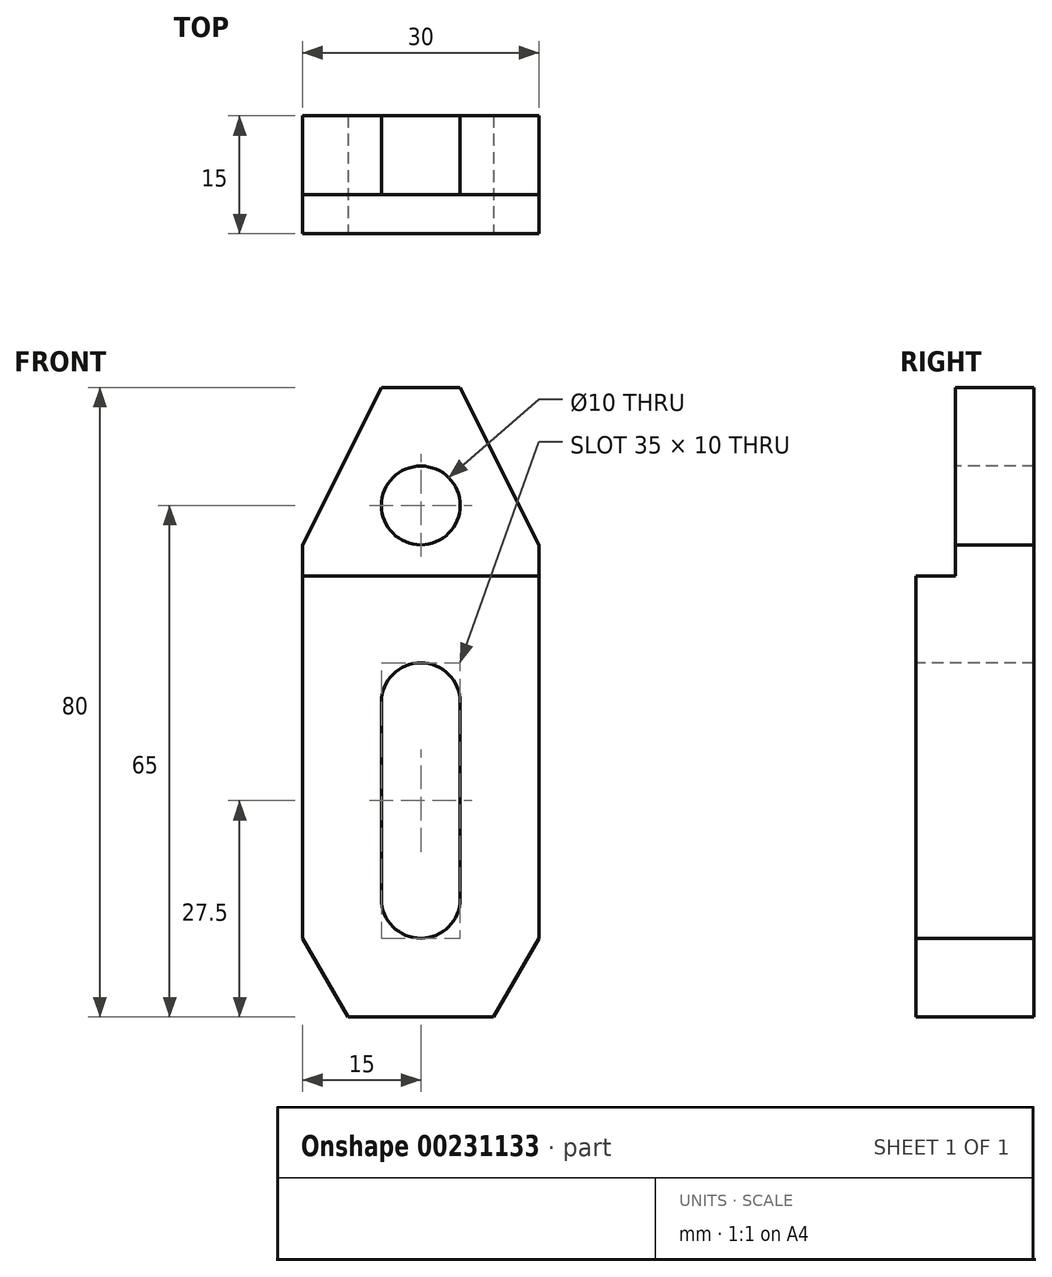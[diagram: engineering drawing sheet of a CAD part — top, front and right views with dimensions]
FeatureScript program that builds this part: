
annotation { "Feature Type Name" : "Feature", "Feature Type Description" : "" }
export const myFeature = defineFeature(function(context is Context, id is Id, definition is map)
    precondition{}
    {
        {
            var Q0;
            Q0=qCreatedBy(makeId("Right.planeOp"),FACE);
            var sketch = newSketch(context, id + "F0", { "sketchPlane" : qUnion([Q0])});
            skLineSegment(sketch, "E0", {"start": v(10, 66) * mm, "end": v(10, 10) * mm});
            skLineSegment(sketch, "E1", {"start": v(10, 10) * mm, "end": v(25, 10) * mm});
            skLineSegment(sketch, "E2", {"start": v(25, 10) * mm, "end": v(25, 90) * mm});
            skLineSegment(sketch, "E3", {"start": v(25, 90) * mm, "end": v(15, 90) * mm});
            skLineSegment(sketch, "E4", {"start": v(15, 90) * mm, "end": v(15, 66) * mm});
            skLineSegment(sketch, "E5", {"start": v(15, 66) * mm, "end": v(10, 66) * mm});
            skSolve(sketch);
        }
        {
            var Q0;
            Q0 = qSketchRegion(id + "F0", true);
            extrude(context, id + "F1", {"entities" : qUnion([Q0]), "depth" : 30 * mm});
        }
        {
            var Q0;
            Q0=makeQuery(id+"F1.opExtrude","SWEPT_FACE",FACE,{"disambiguationData":[OSD([sQuery(id+"F0.wireOp",EDGE,"E0")])]});
            var sketch = newSketch(context, id + "F2", { "sketchPlane" : qUnion([Q0])});
            skLineSegment(sketch, "E6.0.0", {"start": v(0, 66) * mm, "end": v(0, 10) * mm, "construction": true});
            skLineSegment(sketch, "E6.0.1", {"start": v(0, 10) * mm, "end": v(30, 10) * mm, "construction": true});
            skLineSegment(sketch, "E6.0.2", {"start": v(30, 10) * mm, "end": v(30, 66) * mm, "construction": true});
            skLineSegment(sketch, "E6.0.3", {"start": v(30, 66) * mm, "end": v(0, 66) * mm, "construction": true});
            skLineSegment(sketch, "E7.0.0", {"start": v(0, 90) * mm, "end": v(0, 66) * mm, "construction": true});
            skLineSegment(sketch, "E7.0.1", {"start": v(0, 66) * mm, "end": v(30, 66) * mm, "construction": true});
            skLineSegment(sketch, "E7.0.2", {"start": v(30, 66) * mm, "end": v(30, 90) * mm, "construction": true});
            skLineSegment(sketch, "E7.0.3", {"start": v(30, 90) * mm, "end": v(0, 90) * mm, "construction": true});
            skLineSegment(sketch, "E8", {"start": v(15, 106.53) * mm, "end": v(15, -4.36) * mm, "construction": true});
            skLineSegment(sketch, "E9", {"start": v(-10.48, 50) * mm, "end": v(45.87, 50) * mm, "construction": true});
            skLineSegment(sketch, "E10", {"start": v(-7.03, 25) * mm, "end": v(50.6, 25) * mm, "construction": true});
            skLineSegment(sketch, "E11", {"start": v(10, 90) * mm, "end": v(0, 70) * mm});
            skLineSegment(sketch, "E12", {"start": v(0, 70) * mm, "end": v(0, 20) * mm});
            skLineSegment(sketch, "E13", {"start": v(0, 20) * mm, "end": v(5.77, 10) * mm});
            skLineSegment(sketch, "E14", {"start": v(5.77, 10) * mm, "end": v(24.23, 10) * mm});
            skLineSegment(sketch, "E15", {"start": v(24.23, 10) * mm, "end": v(30, 20) * mm});
            skLineSegment(sketch, "E16", {"start": v(30, 20) * mm, "end": v(30, 70) * mm});
            skLineSegment(sketch, "E17", {"start": v(30, 70) * mm, "end": v(20, 90) * mm});
            skLineSegment(sketch, "E18", {"start": v(20, 90) * mm, "end": v(10, 90) * mm});
            skPoint(sketch, "E19", {"position": v(15, 90) * mm});
            skPoint(sketch, "E20", {"position": v(15, 10) * mm});
            skLineSegment(sketch, "E21", {"start": v(10.27, 75) * mm, "end": v(37.52, 75) * mm, "construction": true});
            skCircle(sketch, "E22", {"center": v(15, 75) * mm, "radius": 5 * mm});
            skArc(sketch, "E23", {"start": v(10, 25) * mm, "mid": v(15, 20) * mm, "end": v(20, 25) * mm});
            skArc(sketch, "E24", {"start": v(20, 50) * mm, "mid": v(15, 55) * mm, "end": v(10, 50) * mm});
            skLineSegment(sketch, "E25", {"start": v(10, 50) * mm, "end": v(10, 25) * mm});
            skLineSegment(sketch, "E26", {"start": v(20, 50) * mm, "end": v(20, 25) * mm});
            skLineSegment(sketch, "E27", {"start": v(10, 90) * mm, "end": v(0, 90) * mm});
            skLineSegment(sketch, "E28", {"start": v(0, 70) * mm, "end": v(0, 90) * mm});
            skLineSegment(sketch, "E29", {"start": v(20, 90) * mm, "end": v(30, 90) * mm});
            skLineSegment(sketch, "E30", {"start": v(30, 70) * mm, "end": v(30, 90) * mm});
            skSolve(sketch);
        }
        {
            var Q0;
            Q0=makeQuery(id+"F2.imprint","IMPRINT",FACE,{"disambiguationData":[TD([[makeQuery(id+"F2.imprint","IMPRINT",EDGE,{"derivedFrom":sQuery(id+"F2.wireOp",EDGE,"E23")}),1.0]])]});
            var Q1;
            Q1=makeQuery(id+"F2.imprint","IMPRINT",FACE,{"disambiguationData":[TD([[makeQuery(id+"F2.imprint","IMPRINT",EDGE,{"derivedFrom":sQuery(id+"F2.wireOp",EDGE,"E22")}),1.0]])]});
            var Q2;
            {var subQ0=sQuery(id+"F2.wireOp",EDGE,"E15");Q2=makeQuery(id+"F2.imprint","IMPRINT",FACE,{"disambiguationData":[TD([[makeQuery(id+"F2.imprint","IMPRINT",EDGE,{"derivedFrom":subQ0}),-1.0]])]});}
            var Q3;
            {var subQ0=sQuery(id+"F2.wireOp",EDGE,"E13");Q3=makeQuery(id+"F2.imprint","IMPRINT",FACE,{"disambiguationData":[TD([[makeQuery(id+"F2.imprint","IMPRINT",EDGE,{"derivedFrom":subQ0}),-1.0]])]});}
            extrude(context, id + "F3", {"entities" : qUnion([Q0, Q1, Q2, Q3]), "operationType" : NewBodyOperationType.REMOVE, "endBound" : BoundingType.THROUGH_ALL, "oppositeDirection" : true, "depth" : 25 * mm});
        }
        {
            var Q0;
            Q0=makeQuery(id+"F2.imprint","IMPRINT",FACE,{"disambiguationData":[TD([[makeQuery(id+"F2.imprint","IMPRINT",EDGE,{"derivedFrom":sQuery(id+"F2.wireOp",EDGE,"E11")}),-1.0]])]});
            var Q1;
            Q1=makeQuery(id+"F2.imprint","IMPRINT",FACE,{"disambiguationData":[TD([[makeQuery(id+"F2.imprint","IMPRINT",EDGE,{"derivedFrom":sQuery(id+"F2.wireOp",EDGE,"E17")}),-1.0]])]});
            extrude(context, id + "F4", {"entities" : qUnion([Q0, Q1]), "operationType" : NewBodyOperationType.REMOVE, "endBound" : BoundingType.THROUGH_ALL, "oppositeDirection" : true, "depth" : 25 * mm});
        }
    });
